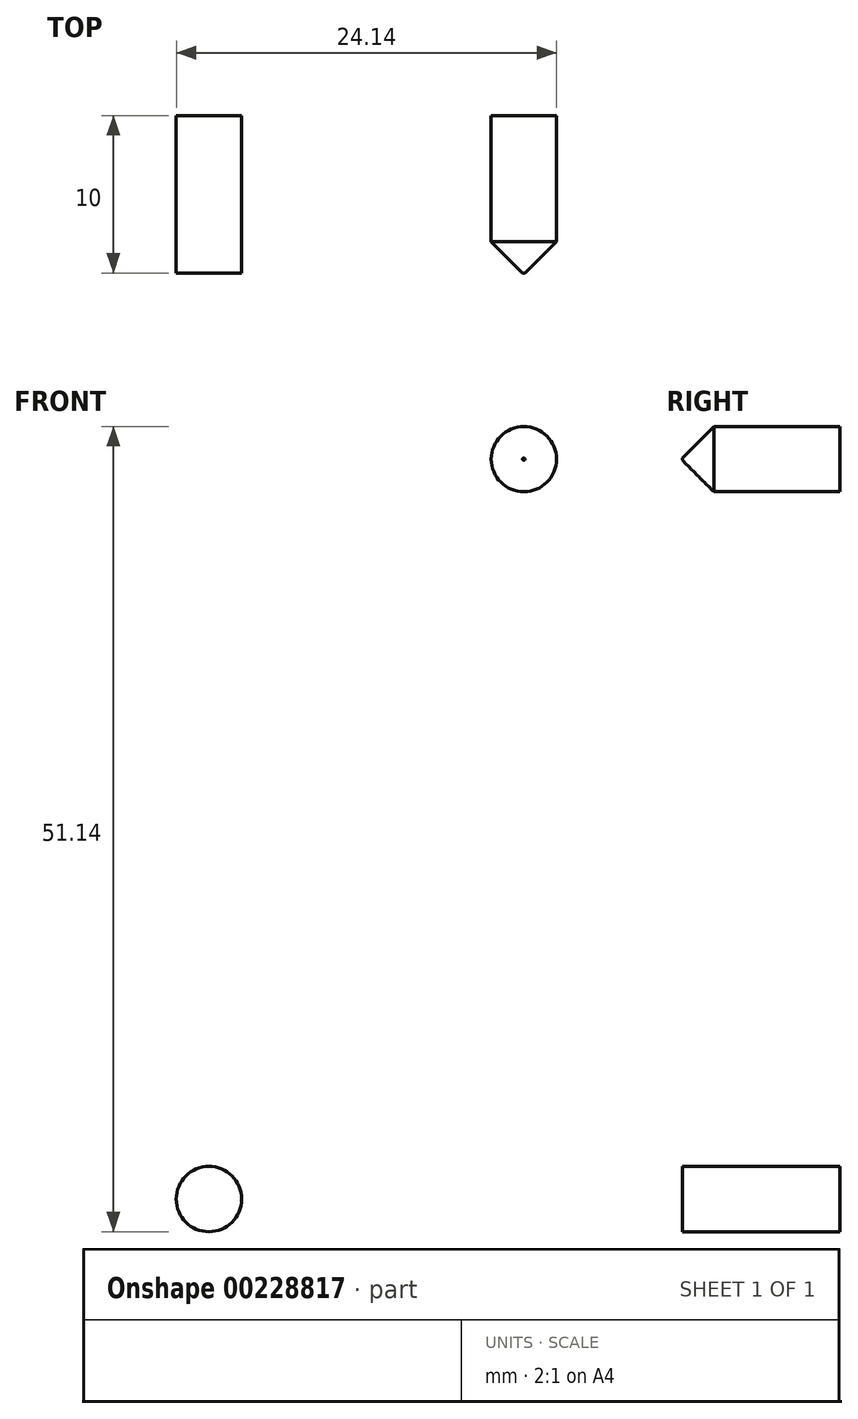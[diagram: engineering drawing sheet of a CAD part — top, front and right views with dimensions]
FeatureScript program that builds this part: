
annotation { "Feature Type Name" : "Feature", "Feature Type Description" : "" }
export const myFeature = defineFeature(function(context is Context, id is Id, definition is map)
    precondition{}
    {
        {
            var Q0;
            Q0=qCreatedBy(makeId("Front.planeOp"),FACE);
            var sketch = newSketch(context, id + "F0", { "sketchPlane" : qUnion([Q0])});
            skLineSegment(sketch, "E0.bottom", {"start": v(-15, 28.5) * mm, "end": v(15, 28.5) * mm});
            skLineSegment(sketch, "E0.top", {"start": v(-15, -28.5) * mm, "end": v(15, -28.5) * mm});
            skLineSegment(sketch, "E0.left", {"start": v(-15, 28.5) * mm, "end": v(-15, -28.5) * mm});
            skLineSegment(sketch, "E0.right", {"start": v(15, 28.5) * mm, "end": v(15, -28.5) * mm});
            skSolve(sketch);
        }
        {
            var Q0;
            Q0 = qSketchRegion(id + "F0", true);
            extrude(context, id + "F1", {"entities" : qUnion([Q0]), "depth" : 5 * mm, "hasSecondDirection" : true, "secondDirectionOppositeDirection" : true, "secondDirectionDepth" : 5 * mm});
        }
        {
            var Q0;
            Q0=makeQuery(id+"F1.opExtrude","SWEPT_EDGE",EDGE,{"disambiguationData":[OSD([sQuery(id+"F0.wireOp",EDGE,"E0.bottom"),sQuery(id+"F0.wireOp",EDGE,"E0.left")])]});
            var Q1;
            Q1=makeQuery(id+"F1.opExtrude","SWEPT_EDGE",EDGE,{"disambiguationData":[OSD([sQuery(id+"F0.wireOp",EDGE,"E0.bottom"),sQuery(id+"F0.wireOp",EDGE,"E0.right")])]});
            var Q2;
            Q2=makeQuery(id+"F1.opExtrude","SWEPT_EDGE",EDGE,{"disambiguationData":[OSD([sQuery(id+"F0.wireOp",EDGE,"E0.top"),sQuery(id+"F0.wireOp",EDGE,"E0.left")])]});
            var Q3;
            Q3=makeQuery(id+"F1.opExtrude","SWEPT_EDGE",EDGE,{"disambiguationData":[OSD([sQuery(id+"F0.wireOp",EDGE,"E0.top"),sQuery(id+"F0.wireOp",EDGE,"E0.right")])]});
            fillet(context, id + "F2", {"entities" : qUnion([Q0, Q1, Q2, Q3]), "radius" : 5 * mm, "tangentPropagation" : true, "allowEdgeOverflow" : false});
        }
        {
            var Q0;
            Q0=makeQuery(id+"F1.opExtrude","CAP_FACE",FACE,{"disambiguationData":[OSD([sQuery(id+"F0.wireOp",EDGE,"E0.bottom"),sQuery(id+"F0.wireOp",EDGE,"E0.top"),sQuery(id+"F0.wireOp",EDGE,"E0.left"),sQuery(id+"F0.wireOp",EDGE,"E0.right")])],"isStart":false});
            var sketch = newSketch(context, id + "F3", { "sketchPlane" : qUnion([Q0])});
            skCircle(sketch, "E1", {"center": v(-10, 23.5) * mm, "radius": 2.07 * mm});
            skCircle(sketch, "E2.MirrorC", {"center": v(-10, -23.5) * mm, "radius": 2.07 * mm});
            skCircle(sketch, "E3.MirrorC", {"center": v(10, 23.5) * mm, "radius": 2.07 * mm});
            skCircle(sketch, "E4.MirrorC", {"center": v(10, -23.5) * mm, "radius": 2.07 * mm});
            skSolve(sketch);
        }
        {
            var Q0;
            Q0=makeQuery(id+"F3.imprint","IMPRINT",FACE,{"disambiguationData":[TD([[makeQuery(id+"F3.imprint","IMPRINT",EDGE,{"derivedFrom":sQuery(id+"F3.wireOp",EDGE,"E1")}),1.0]])]});
            var Q1;
            Q1=makeQuery(id+"F3.imprint","IMPRINT",FACE,{"disambiguationData":[TD([[makeQuery(id+"F3.imprint","IMPRINT",EDGE,{"derivedFrom":sQuery(id+"F3.wireOp",EDGE,"E3.MirrorC")}),-1.0]])]});
            var Q2;
            Q2=makeQuery(id+"F3.imprint","IMPRINT",FACE,{"disambiguationData":[TD([[makeQuery(id+"F3.imprint","IMPRINT",EDGE,{"derivedFrom":sQuery(id+"F3.wireOp",EDGE,"E2.MirrorC")}),-1.0]])]});
            var Q3;
            Q3=makeQuery(id+"F3.imprint","IMPRINT",FACE,{"disambiguationData":[TD([[makeQuery(id+"F3.imprint","IMPRINT",EDGE,{"derivedFrom":sQuery(id+"F3.wireOp",EDGE,"E4.MirrorC")}),1.0]])]});
            extrude(context, id + "F4", {"entities" : qUnion([Q0, Q1, Q2, Q3]), "operationType" : NewBodyOperationType.REMOVE, "endBound" : BoundingType.THROUGH_ALL, "oppositeDirection" : true, "depth" : 25 * mm});
        }
        {
            var Q0;
            Q0=makeQuery(id+"F4.boolean.opBoolean","COPY",EDGE,{"derivedFrom":makeQuery(id+"F4.opExtrude","CAP_EDGE",EDGE,{"disambiguationData":[OSD([sQuery(id+"F3.wireOp",EDGE,"E1")])],"isStart":true})});
            var Q1;
            Q1=makeQuery(id+"F4.boolean.opBoolean","COPY",EDGE,{"derivedFrom":makeQuery(id+"F4.opExtrude","CAP_EDGE",EDGE,{"disambiguationData":[OSD([sQuery(id+"F3.wireOp",EDGE,"E3.MirrorC")])],"isStart":true})});
            var Q2;
            Q2=makeQuery(id+"F4.boolean.opBoolean","COPY",EDGE,{"derivedFrom":makeQuery(id+"F4.opExtrude","CAP_EDGE",EDGE,{"disambiguationData":[OSD([sQuery(id+"F3.wireOp",EDGE,"E2.MirrorC")])],"isStart":true})});
            var Q3;
            Q3=makeQuery(id+"F4.boolean.opBoolean","COPY",EDGE,{"derivedFrom":makeQuery(id+"F4.opExtrude","CAP_EDGE",EDGE,{"disambiguationData":[OSD([sQuery(id+"F3.wireOp",EDGE,"E4.MirrorC")])],"isStart":true})});
            chamfer(context, id + "F5", {"entities" : qUnion([Q0, Q1, Q2, Q3]), "width" : 2 * mm, "tangentPropagation" : true});
        }
    });
